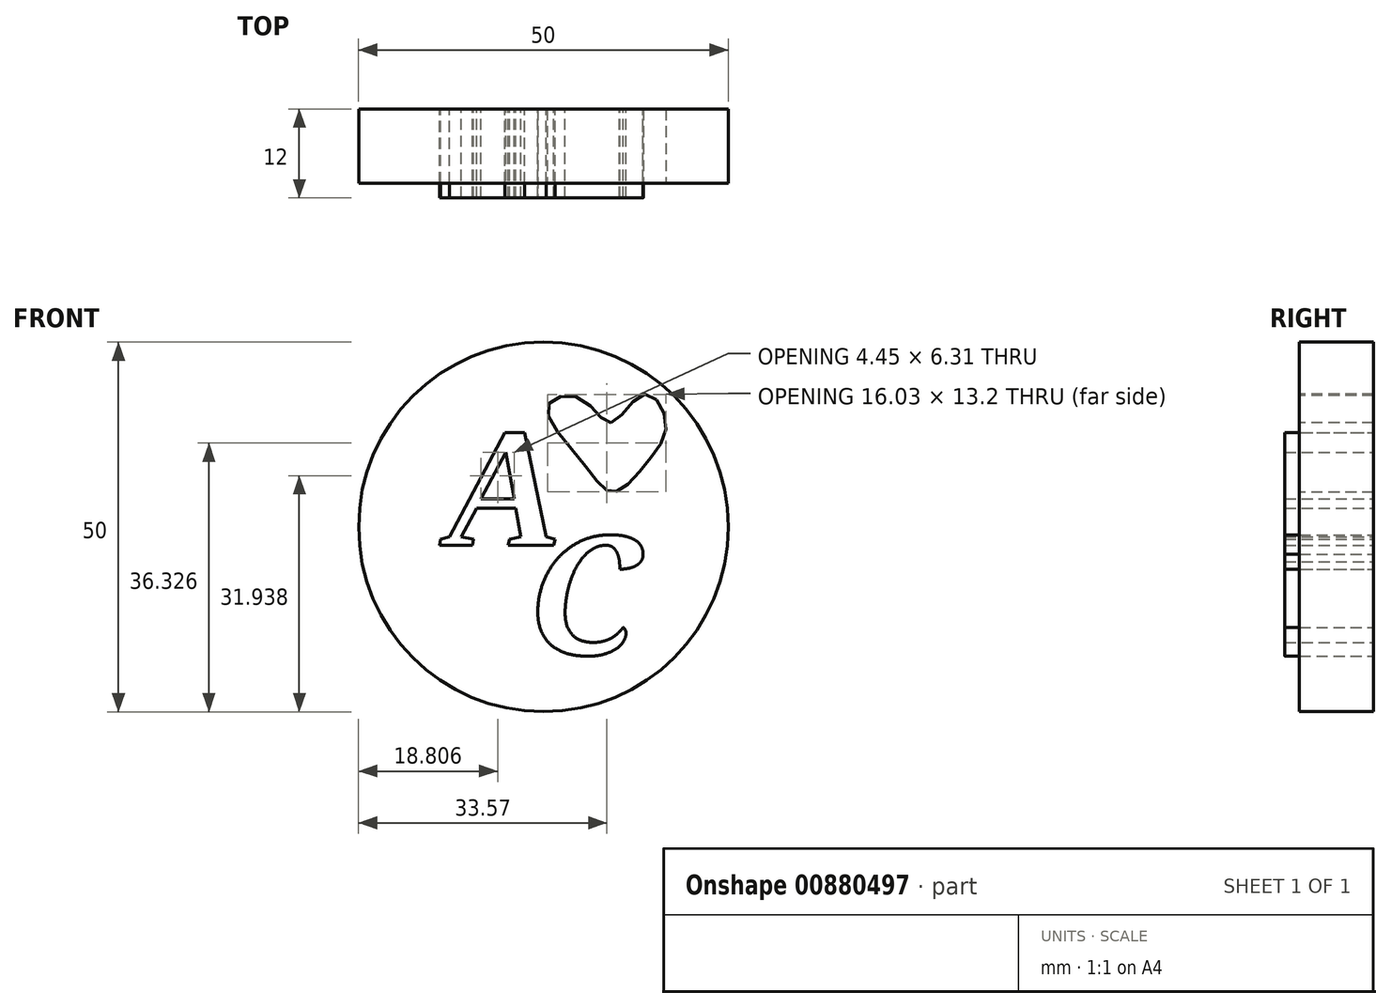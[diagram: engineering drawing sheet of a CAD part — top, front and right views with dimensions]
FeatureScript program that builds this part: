
annotation { "Feature Type Name" : "Feature", "Feature Type Description" : "" }
export const myFeature = defineFeature(function(context is Context, id is Id, definition is map)
    precondition{}
    {
        {
            var Q0;
            Q0=qCreatedBy(makeId("Front.planeOp"),FACE);
            var sketch = newSketch(context, id + "F0", { "sketchPlane" : qUnion([Q0])});
            skCircle(sketch, "E0", {"center": v(-35.97, -8.43) * mm, "radius": 25 * mm});
            skSolve(sketch);
        }
        {
            var Q0;
            Q0 = qSketchRegion(id + "F0", true);
            extrude(context, id + "F1", {"entities" : qUnion([Q0]), "depth" : 10 * mm, "offsetDistance" : 25 * mm});
        }
        {
            var Q0;
            Q0=qCreatedBy(makeId("Front.planeOp"),FACE);
            var sketch = newSketch(context, id + "F2", { "sketchPlane" : qUnion([Q0])});
            skText(sketch, "E1", { "text": "A", "fontName": "Tinos-BoldItalic.ttf"});
            skPoint(sketch, "E2.endSnap0", {"position": v(-31.78, -2.62) * mm});
            const initialGuessF2  = {"E1": [-0.04882, -0.01091, 1, 0, 0.01658]};
            skSetInitialGuess(sketch, initialGuessF2);
            skSolve(sketch);
        }
        {
            var Q0;
            Q0 = qSketchRegion(id + "F2", true);
            extrude(context, id + "F3", {"entities" : qUnion([Q0]), "depth" : 12 * mm, "offsetDistance" : 25 * mm});
        }
        {
            var Q0;
            Q0=qCreatedBy(makeId("Front.planeOp"),FACE);
            var sketch = newSketch(context, id + "F4", { "sketchPlane" : qUnion([Q0])});
            skText(sketch, "E3", { "text": "C", "fontName": "NotoSerif-BoldItalic.ttf"});
            const initialGuessF4  = {"E3": [-0.03814, -0.0257, 1, 0, 0.01603]};
            skSetInitialGuess(sketch, initialGuessF4);
            skSolve(sketch);
        }
        {
            var Q0;
            Q0 = qSketchRegion(id + "F4", true);
            extrude(context, id + "F5", {"entities" : qUnion([Q0]), "depth" : 12 * mm, "offsetDistance" : 25 * mm});
        }
        {
            var Q0;
            Q0=makeQuery(id+"F1.opExtrude","CAP_FACE",FACE,{"disambiguationData":[OSD([sQuery(id+"F0.wireOp",EDGE,"E0")])],"isStart":false});
            var sketch = newSketch(context, id + "F6", { "sketchPlane" : qUnion([Q0])});
            skFitSpline(sketch, "E4", {"points": [v(-26.85, 5.64) * mm, v(-30.98, 8.95) * mm, v(-35.38, 7.85) * mm, v(-30.43, 0) * mm, v(-26.57, -3.72) * mm, v(-22.17, 0) * mm, v(-19.41, 5.92) * mm, v(-22.44, 9.5) * mm, v(-26.85, 5.64) * mm]});
            skSolve(sketch);
        }
        {
            var Q0;
            Q0 = qSketchRegion(id + "F6", true);
            extrude(context, id + "F7", {"entities" : qUnion([Q0]), "operationType" : NewBodyOperationType.REMOVE, "oppositeDirection" : true, "depth" : 10 * mm, "offsetDistance" : 25 * mm});
        }
    });
